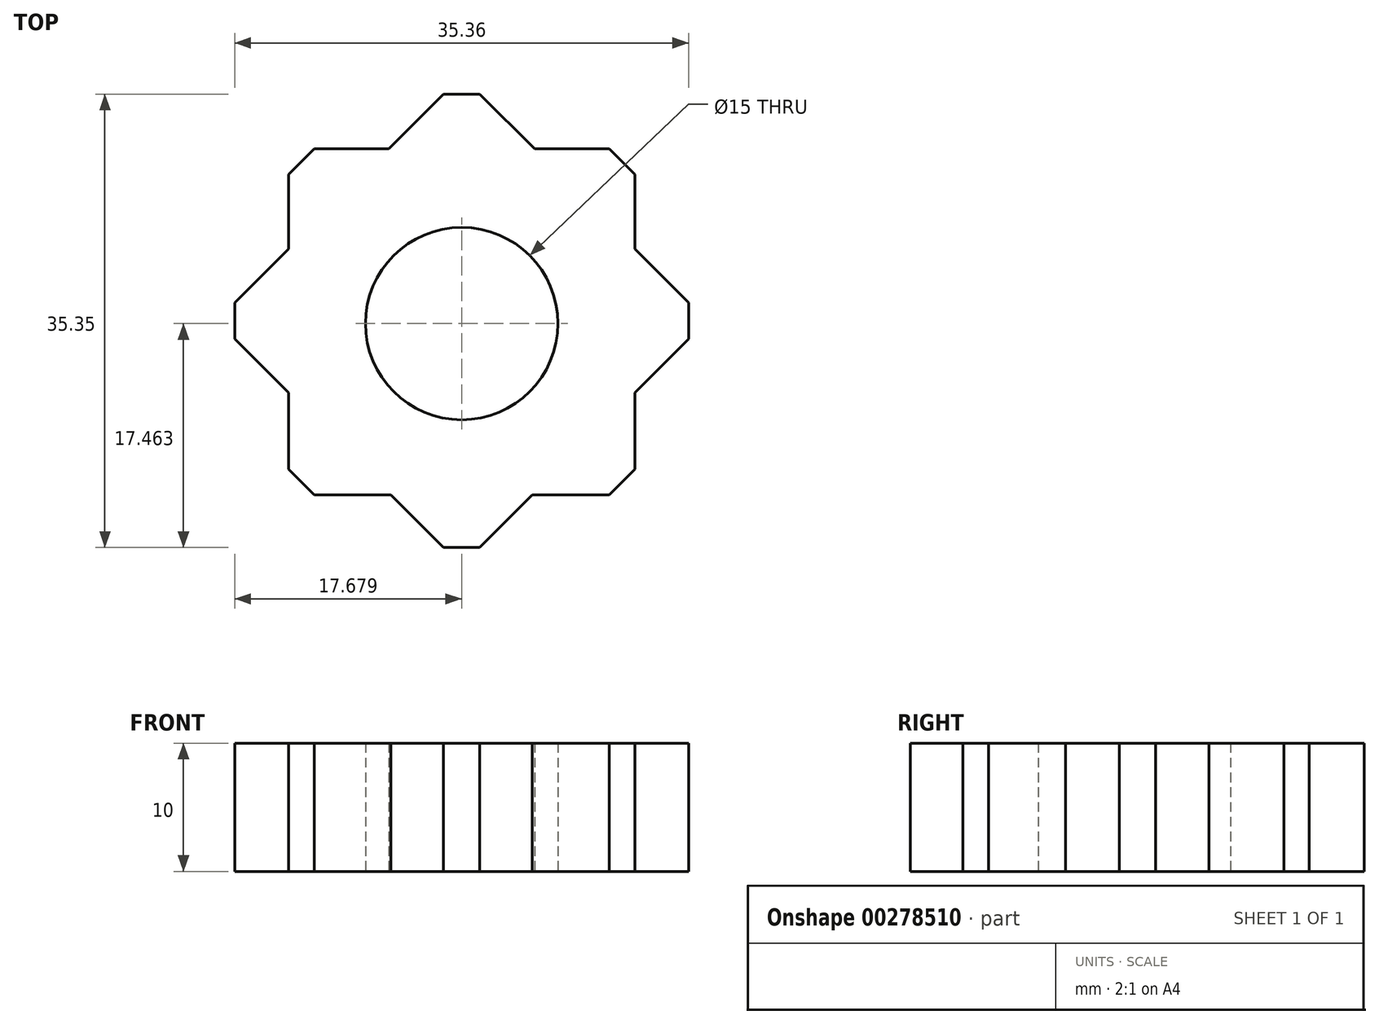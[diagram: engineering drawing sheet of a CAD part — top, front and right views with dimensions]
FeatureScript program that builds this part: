
annotation { "Feature Type Name" : "Feature", "Feature Type Description" : "" }
export const myFeature = defineFeature(function(context is Context, id is Id, definition is map)
    precondition{}
    {
        {
            var Q0;
            Q0=qCreatedBy(makeId("Top.planeOp"),FACE);
            var sketch = newSketch(context, id + "F0", { "sketchPlane" : qUnion([Q0])});
            skLineSegment(sketch, "E0.bottom", {"start": v(-36.78, 36.48) * mm, "end": v(-9.78, 36.48) * mm});
            skLineSegment(sketch, "E0.top", {"start": v(-36.78, 9.48) * mm, "end": v(-9.78, 9.48) * mm});
            skLineSegment(sketch, "E0.left", {"start": v(-36.78, 36.48) * mm, "end": v(-36.78, 9.48) * mm});
            skLineSegment(sketch, "E0.right", {"start": v(-9.78, 36.48) * mm, "end": v(-9.78, 9.48) * mm});
            skLineSegment(sketch, "E1", {"start": v(-42.37, 23.07) * mm, "end": v(-23.28, 3.97) * mm});
            skPoint(sketch, "E1.endSnap0", {"position": v(-23.28, 9.48) * mm});
            skLineSegment(sketch, "E2", {"start": v(-23.28, 3.97) * mm, "end": v(-4.19, 23.07) * mm});
            skLineSegment(sketch, "E3", {"start": v(-4.19, 23.07) * mm, "end": v(-23.28, 42.16) * mm});
            skLineSegment(sketch, "E4", {"start": v(-23.28, 42.16) * mm, "end": v(-42.37, 23.07) * mm});
            skPoint(sketch, "E5", {"position": v(-23.28, 36.48) * mm});
            skCircle(sketch, "E6", {"center": v(-23.28, 22.85) * mm, "radius": 7.5 * mm});
            skSolve(sketch);
        }
        {
            var Q0;
            {var subQ0=sQuery(id+"F0.wireOp",EDGE,"E4");var subQ1=sQuery(id+"F0.wireOp",EDGE,"E0.bottom");var subQ2=makeQuery(id+"F0.imprint","INTERSECT",VERTEX,{"derivedFrom":[subQ1,subQ0]});Q0=makeQuery(id+"F0.imprint","IMPRINT",FACE,{"disambiguationData":[TD([[makeQuery(id+"F0.imprint","IMPRINT",EDGE,{"disambiguationData":[TD([[subQ2,-1.0]])],"derivedFrom":subQ1}),1.0]])]});}
            var Q1;
            {var subQ0=sQuery(id+"F0.wireOp",EDGE,"E3");var subQ1=sQuery(id+"F0.wireOp",EDGE,"E0.right");var subQ2=makeQuery(id+"F0.imprint","INTERSECT",VERTEX,{"derivedFrom":[subQ1,subQ0]});Q1=makeQuery(id+"F0.imprint","IMPRINT",FACE,{"disambiguationData":[TD([[makeQuery(id+"F0.imprint","IMPRINT",EDGE,{"disambiguationData":[TD([[subQ2,-1.0]])],"derivedFrom":subQ1}),1.0]])]});}
            var Q2;
            {var subQ0=sQuery(id+"F0.wireOp",EDGE,"E1");var subQ1=sQuery(id+"F0.wireOp",EDGE,"E0.top");var subQ2=makeQuery(id+"F0.imprint","INTERSECT",VERTEX,{"derivedFrom":[subQ1,subQ0]});Q2=makeQuery(id+"F0.imprint","IMPRINT",FACE,{"disambiguationData":[TD([[makeQuery(id+"F0.imprint","IMPRINT",EDGE,{"disambiguationData":[TD([[subQ2,-1.0]])],"derivedFrom":subQ1}),-1.0]])]});}
            var Q3;
            Q3=makeQuery(id+"F0.imprint","IMPRINT",FACE,{"disambiguationData":[TD([[makeQuery(id+"F0.imprint","IMPRINT",EDGE,{"derivedFrom":sQuery(id+"F0.wireOp",EDGE,"E6")}),-1.0]])]});
            var Q4;
            {var subQ0=sQuery(id+"F0.wireOp",EDGE,"E4");var subQ1=sQuery(id+"F0.wireOp",EDGE,"E0.left");var subQ2=makeQuery(id+"F0.imprint","INTERSECT",VERTEX,{"derivedFrom":[subQ1,subQ0]});Q4=makeQuery(id+"F0.imprint","IMPRINT",FACE,{"disambiguationData":[TD([[makeQuery(id+"F0.imprint","IMPRINT",EDGE,{"disambiguationData":[TD([[subQ2,-1.0]])],"derivedFrom":subQ1}),-1.0]])]});}
            var Q5;
            {var subQ0=sQuery(id+"F0.wireOp",EDGE,"E0.right");var subQ1=sQuery(id+"F0.wireOp",EDGE,"E0.bottom");var subQ2=makeQuery(id+"F0.imprint","INTERSECT",VERTEX,{"derivedFrom":[subQ1,subQ0]});Q5=makeQuery(id+"F0.imprint","IMPRINT",FACE,{"disambiguationData":[TD([[makeQuery(id+"F0.imprint","IMPRINT",EDGE,{"disambiguationData":[TD([[subQ2,1.0]])],"derivedFrom":subQ1}),-1.0]])]});}
            var Q6;
            {var subQ0=sQuery(id+"F0.wireOp",EDGE,"E0.left");var subQ1=sQuery(id+"F0.wireOp",EDGE,"E0.bottom");var subQ2=makeQuery(id+"F0.imprint","INTERSECT",VERTEX,{"derivedFrom":[subQ1,subQ0]});Q6=makeQuery(id+"F0.imprint","IMPRINT",FACE,{"disambiguationData":[TD([[makeQuery(id+"F0.imprint","IMPRINT",EDGE,{"disambiguationData":[TD([[subQ2,-1.0]])],"derivedFrom":subQ1}),-1.0]])]});}
            var Q7;
            {var subQ0=sQuery(id+"F0.wireOp",EDGE,"E0.left");var subQ1=sQuery(id+"F0.wireOp",EDGE,"E0.top");var subQ2=makeQuery(id+"F0.imprint","INTERSECT",VERTEX,{"derivedFrom":[subQ1,subQ0]});Q7=makeQuery(id+"F0.imprint","IMPRINT",FACE,{"disambiguationData":[TD([[makeQuery(id+"F0.imprint","IMPRINT",EDGE,{"disambiguationData":[TD([[subQ2,-1.0]])],"derivedFrom":subQ1}),1.0]])]});}
            var Q8;
            {var subQ0=sQuery(id+"F0.wireOp",EDGE,"E0.right");var subQ1=sQuery(id+"F0.wireOp",EDGE,"E0.top");var subQ2=makeQuery(id+"F0.imprint","INTERSECT",VERTEX,{"derivedFrom":[subQ1,subQ0]});Q8=makeQuery(id+"F0.imprint","IMPRINT",FACE,{"disambiguationData":[TD([[makeQuery(id+"F0.imprint","IMPRINT",EDGE,{"disambiguationData":[TD([[subQ2,1.0]])],"derivedFrom":subQ1}),1.0]])]});}
            extrude(context, id + "F1", {"entities" : qUnion([Q0, Q1, Q2, Q3, Q4, Q5, Q6, Q7, Q8]), "depth" : 10 * mm});
        }
        {
            var Q0;
            Q0=makeQuery(id+"F1.opExtrude","SWEPT_EDGE",EDGE,{"disambiguationData":[OSD([sQuery(id+"F0.wireOp",EDGE,"E2"),sQuery(id+"F0.wireOp",EDGE,"E3")])]});
            chamfer(context, id + "F2", {"entities" : qUnion([Q0]), "width" : 2 * mm, "tangentPropagation" : true});
        }
        {
            var Q0;
            Q0=makeQuery(id+"F1.opExtrude","SWEPT_EDGE",EDGE,{"disambiguationData":[OSD([sQuery(id+"F0.wireOp",EDGE,"E0.top"),sQuery(id+"F0.wireOp",EDGE,"E0.right")])]});
            var Q1;
            Q1=makeQuery(id+"F1.opExtrude","SWEPT_EDGE",EDGE,{"disambiguationData":[OSD([sQuery(id+"F0.wireOp",EDGE,"E1"),sQuery(id+"F0.wireOp",EDGE,"E2")])]});
            var Q2;
            Q2=makeQuery(id+"F1.opExtrude","SWEPT_EDGE",EDGE,{"disambiguationData":[OSD([sQuery(id+"F0.wireOp",EDGE,"E0.top"),sQuery(id+"F0.wireOp",EDGE,"E0.left")])]});
            var Q3;
            Q3=makeQuery(id+"F1.opExtrude","SWEPT_EDGE",EDGE,{"disambiguationData":[OSD([sQuery(id+"F0.wireOp",EDGE,"E0.bottom"),sQuery(id+"F0.wireOp",EDGE,"E0.right")])]});
            var Q4;
            Q4=makeQuery(id+"F1.opExtrude","SWEPT_EDGE",EDGE,{"disambiguationData":[OSD([sQuery(id+"F0.wireOp",EDGE,"E3"),sQuery(id+"F0.wireOp",EDGE,"E4")])]});
            var Q5;
            Q5=makeQuery(id+"F1.opExtrude","SWEPT_EDGE",EDGE,{"disambiguationData":[OSD([sQuery(id+"F0.wireOp",EDGE,"E0.bottom"),sQuery(id+"F0.wireOp",EDGE,"E0.left")])]});
            var Q6;
            Q6=makeQuery(id+"F1.opExtrude","SWEPT_EDGE",EDGE,{"disambiguationData":[OSD([sQuery(id+"F0.wireOp",EDGE,"E1"),sQuery(id+"F0.wireOp",EDGE,"E4")])]});
            chamfer(context, id + "F3", {"entities" : qUnion([Q0, Q1, Q2, Q3, Q4, Q5, Q6]), "width" : 2 * mm, "tangentPropagation" : true});
        }
    });
